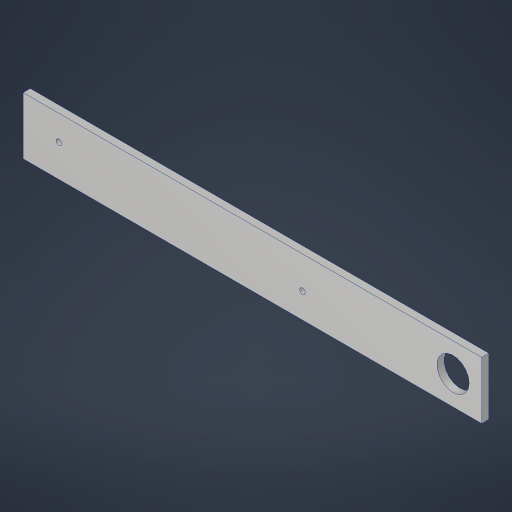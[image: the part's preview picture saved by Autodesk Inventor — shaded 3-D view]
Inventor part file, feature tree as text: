
AUTODESK INVENTOR PART (.ipt)
format: ipt  version: 2023.4 (Build 274418000, 418)  size: 181,760 bytes
history: native  units: in
note: dims shown in document units (in); Inventor stores cm internally (conversion verified against a paired STEP export)
features: sketch x1, extrude x1, hole x1
ambient origin geometry x8: Origin, YZ Plane, XZ Plane, XY Plane, X Axis, Y Axis, Z Axis, Center Point
bodies: Solid1 (feature_tree)
feature tree (3):
  sketch  "Sketch1"  dims[d0=16.0in d1=2.0in d2=1.125in d3=1.125in d4=7.375in d5=24.0in d6=8.5in d7=0.25in d8=1.25in d9=0.875in d10=1.125in d11=1.0in d12=0.25in d13=0.0in d14=0.201in d15=0.75in d16=0.385in d17=0.25in d18=0.5635in d19=1.0in d20=0.8108in]
  extrude  "Extrusion1"  Depth=2.0in
  hole  "Hole1"  [1 undecoded]
note: 1 required parameter value undecoded (feature->parameter linkage not recoverable at this tier; creation-order binding heuristic only, values carry confidence <= 0.55)
